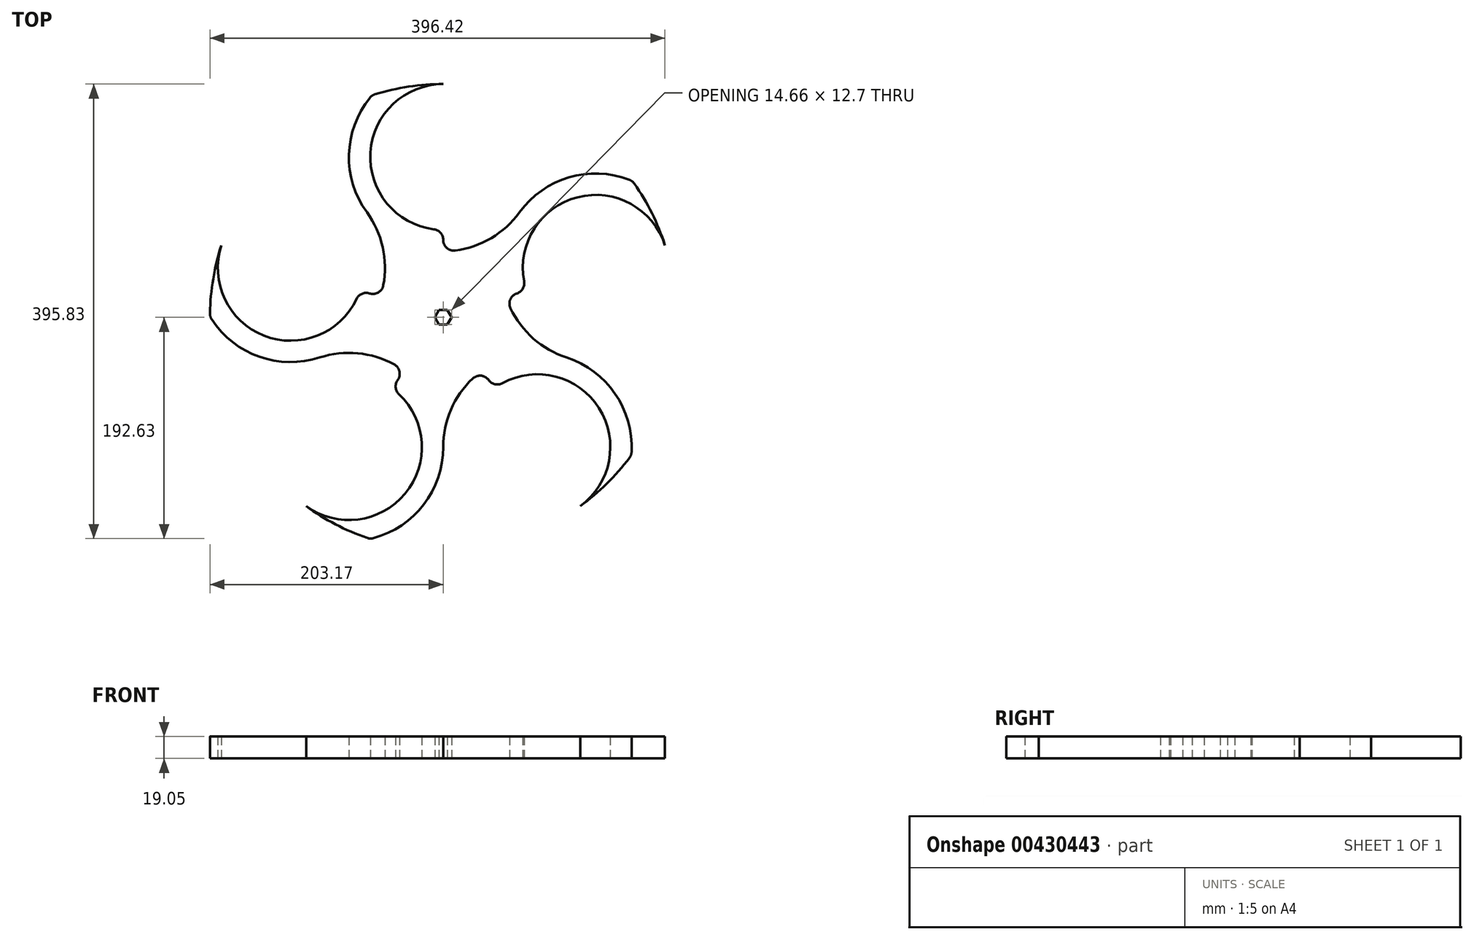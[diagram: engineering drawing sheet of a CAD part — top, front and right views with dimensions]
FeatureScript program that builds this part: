
annotation { "Feature Type Name" : "Feature", "Feature Type Description" : "" }
export const myFeature = defineFeature(function(context is Context, id is Id, definition is map)
    precondition{}
    {
        {
            var Q0;
            Q0=qCreatedBy(makeId("Top.planeOp"),FACE);
            var sketch = newSketch(context, id + "F0", { "sketchPlane" : qUnion([Q0])});
            skCircle(sketch, "E0", {"center": v(0, 0) * mm, "radius": 203.2 * mm});
            skCircle(sketch, "E1.cCircle", {"center": v(0, 0) * mm, "radius": 6.35 * mm, "construction": true});
            skLineSegment(sketch, "E1.0", {"start": v(-3.67, 6.35) * mm, "end": v(3.67, 6.35) * mm});
            skLineSegment(sketch, "E1.1", {"start": v(3.67, 6.35) * mm, "end": v(7.33, 0) * mm});
            skLineSegment(sketch, "E1.2", {"start": v(7.33, 0) * mm, "end": v(3.67, -6.35) * mm});
            skLineSegment(sketch, "E1.3", {"start": v(3.67, -6.35) * mm, "end": v(-3.67, -6.35) * mm});
            skLineSegment(sketch, "E1.4", {"start": v(-3.67, -6.35) * mm, "end": v(-7.33, 0) * mm});
            skLineSegment(sketch, "E1.5", {"start": v(-7.33, 0) * mm, "end": v(-3.67, 6.35) * mm});
            skPoint(sketch, "E1.0.midPoint", {"position": v(0, 6.35) * mm});
            skCircle(sketch, "E2", {"center": v(0, 139.7) * mm, "radius": 63.5 * mm});
            skLineSegment(sketch, "E3", {"start": v(0, 203.2) * mm, "end": v(0, 0) * mm});
            skCircle(sketch, "E4", {"center": v(0, 139.7) * mm, "radius": 82.11 * mm});
            skLineSegment(sketch, "E5.1.0", {"start": v(-193.25, 62.8) * mm, "end": v(0, 0) * mm});
            skCircle(sketch, "E5.1.1", {"center": v(-132.86, 43.17) * mm, "radius": 63.5 * mm});
            skCircle(sketch, "E5.1.2", {"center": v(-132.86, 43.17) * mm, "radius": 82.11 * mm});
            skLineSegment(sketch, "E5.2.0", {"start": v(-119.44, -164.4) * mm, "end": v(0, 0) * mm});
            skCircle(sketch, "E5.2.1", {"center": v(-82.11, -113.02) * mm, "radius": 63.5 * mm});
            skCircle(sketch, "E5.2.2", {"center": v(-82.11, -113.02) * mm, "radius": 82.11 * mm});
            skLineSegment(sketch, "E5.3.0", {"start": v(119.44, -164.4) * mm, "end": v(0, 0) * mm});
            skCircle(sketch, "E5.3.1", {"center": v(82.11, -113.02) * mm, "radius": 63.5 * mm});
            skCircle(sketch, "E5.3.2", {"center": v(82.11, -113.02) * mm, "radius": 82.11 * mm});
            skLineSegment(sketch, "E5.4.0", {"start": v(193.25, 62.8) * mm, "end": v(0, 0) * mm});
            skCircle(sketch, "E5.4.1", {"center": v(132.86, 43.17) * mm, "radius": 63.5 * mm});
            skCircle(sketch, "E5.4.2", {"center": v(132.86, 43.17) * mm, "radius": 82.11 * mm});
            skSolve(sketch);
        }
        {
            var Q0;
            {var subQ4=sQuery(id+"F0.wireOp",EDGE,"E3");var subQ5=sQuery(id+"F0.wireOp",EDGE,"E2");var subQ7=makeQuery(id+"F0.imprint","INTERSECT",VERTEX,{"derivedFrom":[subQ5,subQ4]});Q0=makeQuery(id+"F0.imprint","IMPRINT",FACE,{"disambiguationData":[TD([[makeQuery(id+"F0.imprint","IMPRINT",EDGE,{"disambiguationData":[TD([[subQ7,-1.0]])],"derivedFrom":subQ4}),-1.0]])]});}
            var Q1;
            {var subQ5=sQuery(id+"F0.wireOp",EDGE,"E1.0");var subQ7=sQuery(id+"F0.wireOp",EDGE,"E1.5");var subQ8=makeQuery(id+"F0.imprint","INTERSECT",VERTEX,{"derivedFrom":[subQ5,subQ7]});Q1=makeQuery(id+"F0.imprint","IMPRINT",FACE,{"disambiguationData":[TD([[makeQuery(id+"F0.imprint","IMPRINT",EDGE,{"disambiguationData":[TD([[subQ8,-1.0]])],"derivedFrom":subQ5}),1.0]])]});}
            var Q2;
            {var subQ5=sQuery(id+"F0.wireOp",EDGE,"E1.0");var subQ7=sQuery(id+"F0.wireOp",EDGE,"E1.1");var subQ8=makeQuery(id+"F0.imprint","INTERSECT",VERTEX,{"derivedFrom":[subQ5,subQ7]});Q2=makeQuery(id+"F0.imprint","IMPRINT",FACE,{"disambiguationData":[TD([[makeQuery(id+"F0.imprint","IMPRINT",EDGE,{"disambiguationData":[TD([[subQ8,1.0]])],"derivedFrom":subQ5}),1.0]])]});}
            var Q3;
            {var subQ5=sQuery(id+"F0.wireOp",EDGE,"E1.2");var subQ8=sQuery(id+"F0.wireOp",EDGE,"E1.1");var subQ11=makeQuery(id+"F0.imprint","INTERSECT",VERTEX,{"derivedFrom":[subQ8,subQ5]});Q3=makeQuery(id+"F0.imprint","IMPRINT",FACE,{"disambiguationData":[TD([[makeQuery(id+"F0.imprint","IMPRINT",EDGE,{"disambiguationData":[TD([[subQ11,1.0]])],"derivedFrom":subQ8}),1.0]])]});}
            var Q4;
            {var subQ1=sQuery(id+"F0.wireOp",EDGE,"E1.3");Q4=makeQuery(id+"F0.imprint","IMPRINT",FACE,{"disambiguationData":[TD([[makeQuery(id+"F0.imprint","IMPRINT",EDGE,{"derivedFrom":subQ1}),1.0]])]});}
            var Q5;
            {var subQ5=sQuery(id+"F0.wireOp",EDGE,"E1.5");var subQ6=sQuery(id+"F0.wireOp",EDGE,"E1.4");var subQ7=makeQuery(id+"F0.imprint","INTERSECT",VERTEX,{"derivedFrom":[subQ6,subQ5]});Q5=makeQuery(id+"F0.imprint","IMPRINT",FACE,{"disambiguationData":[TD([[makeQuery(id+"F0.imprint","IMPRINT",EDGE,{"disambiguationData":[TD([[subQ7,1.0]])],"derivedFrom":subQ6}),1.0]])]});}
            var Q6;
            {var subQ4=sQuery(id+"F0.wireOp",EDGE,"E5.1.1");var subQ5=sQuery(id+"F0.wireOp",EDGE,"E5.1.0");var subQ7=makeQuery(id+"F0.imprint","INTERSECT",VERTEX,{"derivedFrom":[subQ5,subQ4]});Q6=makeQuery(id+"F0.imprint","IMPRINT",FACE,{"disambiguationData":[TD([[makeQuery(id+"F0.imprint","IMPRINT",EDGE,{"disambiguationData":[TD([[subQ7,-1.0]])],"derivedFrom":subQ5}),-1.0]])]});}
            var Q7;
            {var subQ0=sQuery(id+"F0.wireOp",EDGE,"E5.2.1");var subQ1=sQuery(id+"F0.wireOp",EDGE,"E5.2.0");var subQ4=makeQuery(id+"F0.imprint","INTERSECT",VERTEX,{"derivedFrom":[subQ1,subQ0]});Q7=makeQuery(id+"F0.imprint","IMPRINT",FACE,{"disambiguationData":[TD([[makeQuery(id+"F0.imprint","IMPRINT",EDGE,{"disambiguationData":[TD([[subQ4,-1.0]])],"derivedFrom":subQ1}),-1.0]])]});}
            var Q8;
            {var subQ4=sQuery(id+"F0.wireOp",EDGE,"E5.3.1");var subQ5=sQuery(id+"F0.wireOp",EDGE,"E5.3.0");var subQ6=makeQuery(id+"F0.imprint","INTERSECT",VERTEX,{"derivedFrom":[subQ5,subQ4]});Q8=makeQuery(id+"F0.imprint","IMPRINT",FACE,{"disambiguationData":[TD([[makeQuery(id+"F0.imprint","IMPRINT",EDGE,{"disambiguationData":[TD([[subQ6,-1.0]])],"derivedFrom":subQ5}),-1.0]])]});}
            var Q9;
            {var subQ4=sQuery(id+"F0.wireOp",EDGE,"E5.4.1");var subQ5=sQuery(id+"F0.wireOp",EDGE,"E5.4.0");var subQ7=makeQuery(id+"F0.imprint","INTERSECT",VERTEX,{"derivedFrom":[subQ5,subQ4]});Q9=makeQuery(id+"F0.imprint","IMPRINT",FACE,{"disambiguationData":[TD([[makeQuery(id+"F0.imprint","IMPRINT",EDGE,{"disambiguationData":[TD([[subQ7,-1.0]])],"derivedFrom":subQ5}),-1.0]])]});}
            extrude(context, id + "F1", {"entities" : qUnion([Q0, Q1, Q2, Q3, Q4, Q5, Q6, Q7, Q8, Q9]), "depth" : 19.05 * mm});
        }
        {
            var Q0;
            Q0=makeQuery(id+"F1.opExtrude","SWEPT_EDGE",EDGE,{"disambiguationData":[OSD([sQuery(id+"F0.wireOp",EDGE,"E5.2.0"),sQuery(id+"F0.wireOp",EDGE,"E5.2.1")])]});
            var Q1;
            Q1=makeQuery(id+"F1.opExtrude","SWEPT_EDGE",EDGE,{"disambiguationData":[OSD([sQuery(id+"F0.wireOp",EDGE,"E5.3.0"),sQuery(id+"F0.wireOp",EDGE,"E5.3.1")])]});
            var Q2;
            Q2=makeQuery(id+"F1.opExtrude","SWEPT_EDGE",EDGE,{"disambiguationData":[OSD([sQuery(id+"F0.wireOp",EDGE,"E5.4.0"),sQuery(id+"F0.wireOp",EDGE,"E5.4.1")])]});
            var Q3;
            Q3=makeQuery(id+"F1.opExtrude","SWEPT_EDGE",EDGE,{"disambiguationData":[OSD([sQuery(id+"F0.wireOp",EDGE,"E2"),sQuery(id+"F0.wireOp",EDGE,"E3")])]});
            var Q4;
            Q4=makeQuery(id+"F1.opExtrude","SWEPT_EDGE",EDGE,{"disambiguationData":[OSD([sQuery(id+"F0.wireOp",EDGE,"E5.1.0"),sQuery(id+"F0.wireOp",EDGE,"E5.1.1")])]});
            var Q5;
            Q5=makeQuery(id+"F1.opExtrude","SWEPT_EDGE",EDGE,{"disambiguationData":[OSD([sQuery(id+"F0.wireOp",EDGE,"E5.1.0"),sQuery(id+"F0.wireOp",EDGE,"E5.1.2")])]});
            var Q6;
            Q6=makeQuery(id+"F1.opExtrude","SWEPT_EDGE",EDGE,{"disambiguationData":[OSD([sQuery(id+"F0.wireOp",EDGE,"E3"),sQuery(id+"F0.wireOp",EDGE,"E4")])]});
            var Q7;
            Q7=makeQuery(id+"F1.opExtrude","SWEPT_EDGE",EDGE,{"disambiguationData":[OSD([sQuery(id+"F0.wireOp",EDGE,"E5.4.0"),sQuery(id+"F0.wireOp",EDGE,"E5.4.2")])]});
            var Q8;
            Q8=makeQuery(id+"F1.opExtrude","SWEPT_EDGE",EDGE,{"disambiguationData":[OSD([sQuery(id+"F0.wireOp",EDGE,"E5.3.0"),sQuery(id+"F0.wireOp",EDGE,"E5.3.2")])]});
            var Q9;
            Q9=makeQuery(id+"F1.opExtrude","SWEPT_EDGE",EDGE,{"disambiguationData":[OSD([sQuery(id+"F0.wireOp",EDGE,"E5.2.0"),sQuery(id+"F0.wireOp",EDGE,"E5.2.2")])]});
            var Q10;
            Q10=makeQuery(id+"F1.opExtrude","SWEPT_EDGE",EDGE,{"disambiguationData":[OSD([sQuery(id+"F0.wireOp",EDGE,"E0"),sQuery(id+"F0.wireOp",EDGE,"E5.2.2")])]});
            var Q11;
            Q11=makeQuery(id+"F1.opExtrude","SWEPT_EDGE",EDGE,{"disambiguationData":[OSD([sQuery(id+"F0.wireOp",EDGE,"E0"),sQuery(id+"F0.wireOp",EDGE,"E5.3.2")])]});
            var Q12;
            Q12=makeQuery(id+"F1.opExtrude","SWEPT_EDGE",EDGE,{"disambiguationData":[OSD([sQuery(id+"F0.wireOp",EDGE,"E0"),sQuery(id+"F0.wireOp",EDGE,"E5.4.2")])]});
            var Q13;
            Q13=makeQuery(id+"F1.opExtrude","SWEPT_EDGE",EDGE,{"disambiguationData":[OSD([sQuery(id+"F0.wireOp",EDGE,"E0"),sQuery(id+"F0.wireOp",EDGE,"E4")])]});
            var Q14;
            Q14=makeQuery(id+"F1.opExtrude","SWEPT_EDGE",EDGE,{"disambiguationData":[OSD([sQuery(id+"F0.wireOp",EDGE,"E0"),sQuery(id+"F0.wireOp",EDGE,"E5.1.2")])]});
            fillet(context, id + "F2", {"entities" : qUnion([Q0, Q1, Q2, Q3, Q4, Q5, Q6, Q7, Q8, Q9, Q10, Q11, Q12, Q13, Q14]), "radius" : 9.27 * mm, "tangentPropagation" : true, "allowEdgeOverflow" : false});
        }
    });
